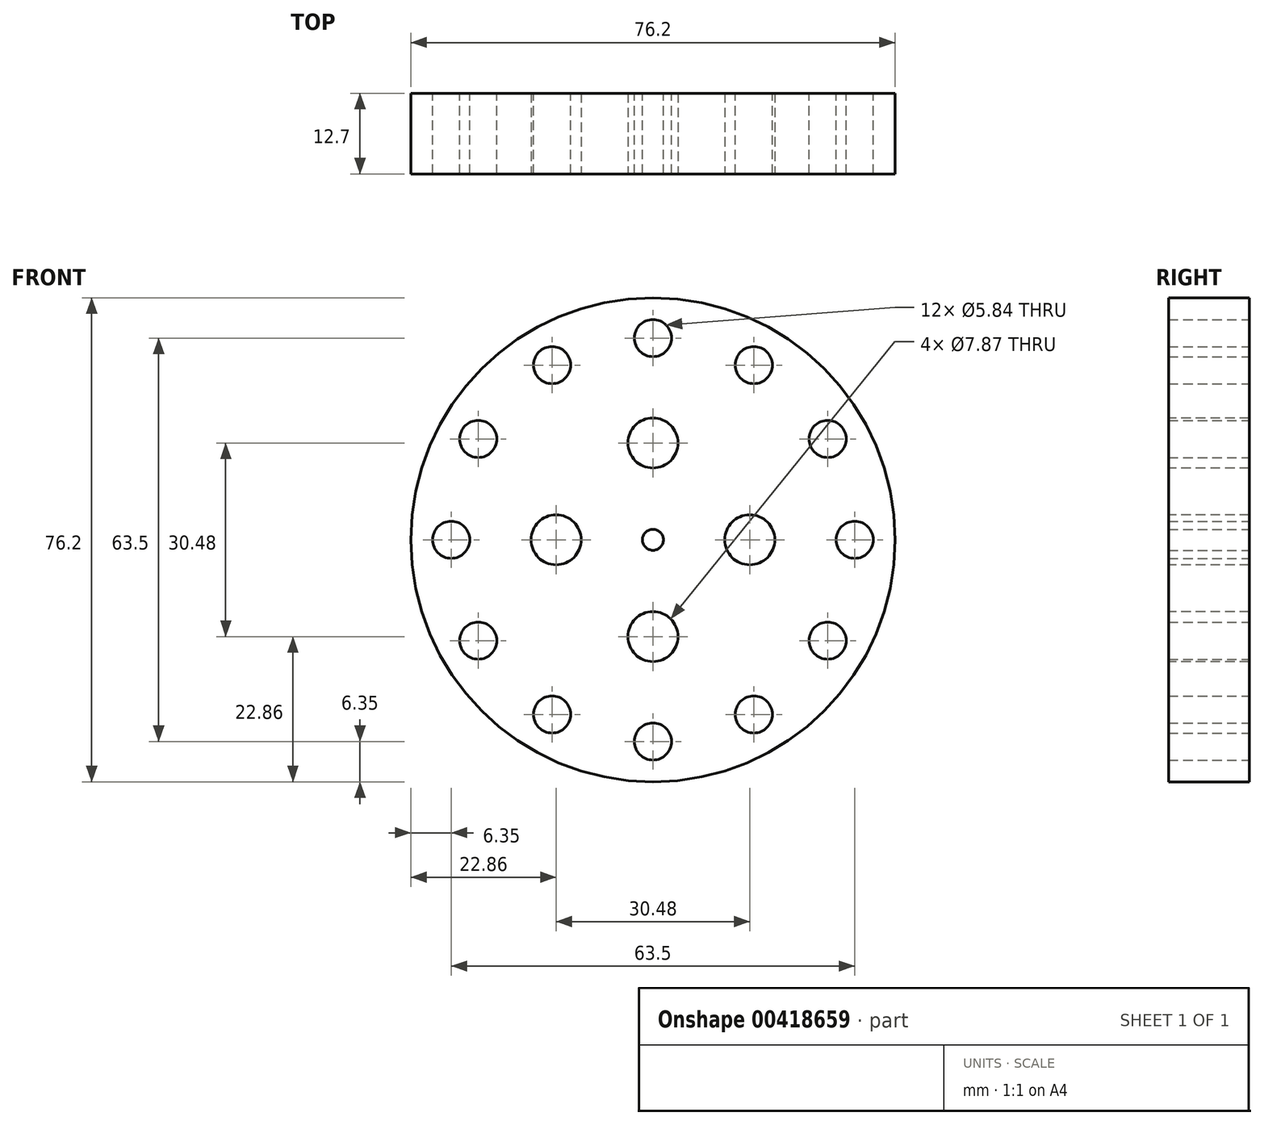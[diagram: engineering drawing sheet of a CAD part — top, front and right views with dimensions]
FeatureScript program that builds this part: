
annotation { "Feature Type Name" : "Feature", "Feature Type Description" : "" }
export const myFeature = defineFeature(function(context is Context, id is Id, definition is map)
    precondition{}
    {
        {
            var Q0;
            Q0=qCreatedBy(makeId("Front.planeOp"),FACE);
            var sketch = newSketch(context, id + "F0", { "sketchPlane" : qUnion([Q0])});
            skCircle(sketch, "E0", {"center": v(0, 0) * mm, "radius": 38.1 * mm});
            skSolve(sketch);
        }
        {
            var Q0;
            Q0=makeQuery(id+"F0.imprint","IMPRINT",FACE,{"disambiguationData":[TD([[makeQuery(id+"F0.imprint","IMPRINT",EDGE,{"derivedFrom":sQuery(id+"F0.wireOp",EDGE,"E0")}),1.0]])]});
            var sketch = newSketch(context, id + "F1", { "sketchPlane" : qUnion([Q0])});
            skCircle(sketch, "E1", {"center": v(0, 0) * mm, "radius": 1.65 * mm});
            skCircle(sketch, "E2", {"center": v(0, -31.75) * mm, "radius": 2.92 * mm});
            skCircle(sketch, "E3.1.0", {"center": v(15.87, -27.5) * mm, "radius": 2.92 * mm});
            skCircle(sketch, "E3.2.0", {"center": v(27.5, -15.88) * mm, "radius": 2.92 * mm});
            skCircle(sketch, "E3.3.0", {"center": v(31.75, 0) * mm, "radius": 2.92 * mm});
            skCircle(sketch, "E3.4.0", {"center": v(27.5, 15.87) * mm, "radius": 2.92 * mm});
            skCircle(sketch, "E3.5.0", {"center": v(15.87, 27.5) * mm, "radius": 2.92 * mm});
            skCircle(sketch, "E3.6.0", {"center": v(0, 31.75) * mm, "radius": 2.92 * mm});
            skCircle(sketch, "E3.7.0", {"center": v(-15.87, 27.5) * mm, "radius": 2.92 * mm});
            skCircle(sketch, "E4.1.8.0", {"center": v(-27.5, 15.88) * mm, "radius": 2.92 * mm});
            skCircle(sketch, "E4.1.9.0", {"center": v(-31.75, 0) * mm, "radius": 2.92 * mm});
            skCircle(sketch, "E5.1.10.0", {"center": v(-27.5, -15.88) * mm, "radius": 2.92 * mm});
            skCircle(sketch, "E5.1.11.0", {"center": v(-15.88, -27.5) * mm, "radius": 2.92 * mm});
            skSolve(sketch);
        }
        {
            var Q0;
            Q0=makeQuery(id+"F1.imprint","IMPRINT",FACE,{"disambiguationData":[TD([[makeQuery(id+"F1.imprint","IMPRINT",EDGE,{"derivedFrom":sQuery(id+"F1.wireOp",EDGE,"E1")}),-1.0]])]});
            extrude(context, id + "F2", {"entities" : qUnion([Q0]), "depth" : 12.7 * mm});
        }
        {
            var Q0;
            Q0=makeQuery(id+"F2.opExtrude","CAP_FACE",FACE,{"disambiguationData":[OSD([sQuery(id+"F0.wireOp",EDGE,"E0"),sQuery(id+"F1.wireOp",EDGE,"E1"),sQuery(id+"F1.wireOp",EDGE,"E2"),sQuery(id+"F1.wireOp",EDGE,"E3.1.0"),sQuery(id+"F1.wireOp",EDGE,"E3.2.0"),sQuery(id+"F1.wireOp",EDGE,"E3.3.0"),sQuery(id+"F1.wireOp",EDGE,"E3.4.0"),sQuery(id+"F1.wireOp",EDGE,"E3.5.0"),sQuery(id+"F1.wireOp",EDGE,"E3.6.0"),sQuery(id+"F1.wireOp",EDGE,"E3.7.0"),sQuery(id+"F1.wireOp",EDGE,"E4.1.8.0"),sQuery(id+"F1.wireOp",EDGE,"E4.1.9.0"),sQuery(id+"F1.wireOp",EDGE,"E4.1.10.0"),sQuery(id+"F1.wireOp",EDGE,"E4.1.11.0"),sQuery(id+"F1.wireOp",EDGE,"E4.1.12.0"),sQuery(id+"F1.wireOp",EDGE,"E4.1.13.0"),sQuery(id+"F1.wireOp",EDGE,"E4.1.14.0"),sQuery(id+"F1.wireOp",EDGE,"E4.1.15.0")])],"isStart":false});
            var sketch = newSketch(context, id + "F3", { "sketchPlane" : qUnion([Q0])});
            skCircle(sketch, "E6", {"center": v(0, 15.24) * mm, "radius": 3.94 * mm});
            skCircle(sketch, "E7", {"center": v(15.24, 0) * mm, "radius": 3.94 * mm});
            skCircle(sketch, "E8", {"center": v(-15.24, 0) * mm, "radius": 3.94 * mm});
            skCircle(sketch, "E9", {"center": v(0, -15.24) * mm, "radius": 3.94 * mm});
            skSolve(sketch);
        }
        {
            var Q0;
            Q0 = qSketchRegion(id + "F3", true);
            extrude(context, id + "F4", {"entities" : qUnion([Q0]), "operationType" : NewBodyOperationType.REMOVE, "oppositeDirection" : true, "depth" : 25.4 * mm});
        }
    });
